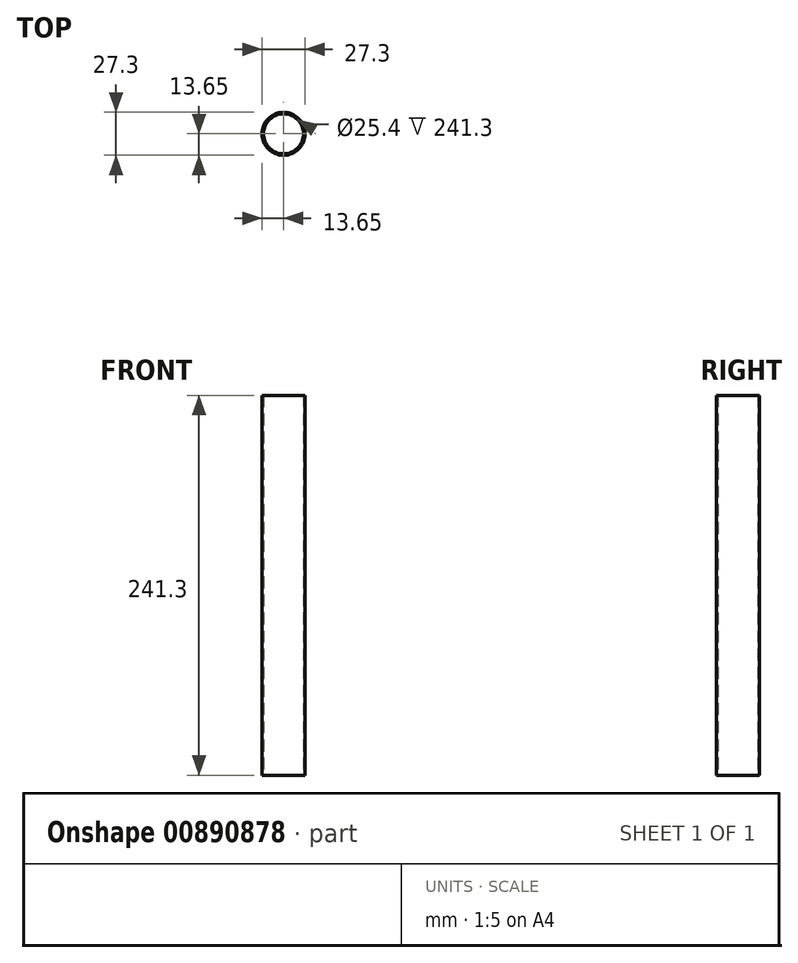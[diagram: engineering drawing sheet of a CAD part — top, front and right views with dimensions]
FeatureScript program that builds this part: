
annotation { "Feature Type Name" : "Feature", "Feature Type Description" : "" }
export const myFeature = defineFeature(function(context is Context, id is Id, definition is map)
    precondition{}
    {
        {
            var Q0;
            Q0=qCreatedBy(makeId("Top.planeOp"),FACE);
            var sketch = newSketch(context, id + "F0", { "sketchPlane" : qUnion([Q0])});
            skCircle(sketch, "E0", {"center": v(0, 0) * mm, "radius": 12.7 * mm});
            skCircle(sketch, "E1", {"center": v(0, 0) * mm, "radius": 13.65 * mm});
            skSolve(sketch);
        }
        {
            var Q0;
            Q0=makeQuery(id+"F0.imprint","IMPRINT",FACE,{"disambiguationData":[TD([[makeQuery(id+"F0.imprint","IMPRINT",EDGE,{"derivedFrom":sQuery(id+"F0.wireOp",EDGE,"E0")}),-1.0]])]});
            extrude(context, id + "F1", {"entities" : qUnion([Q0]), "depth" : 241.3 * mm, "offsetDistance" : 25.4 * mm});
        }
    });
